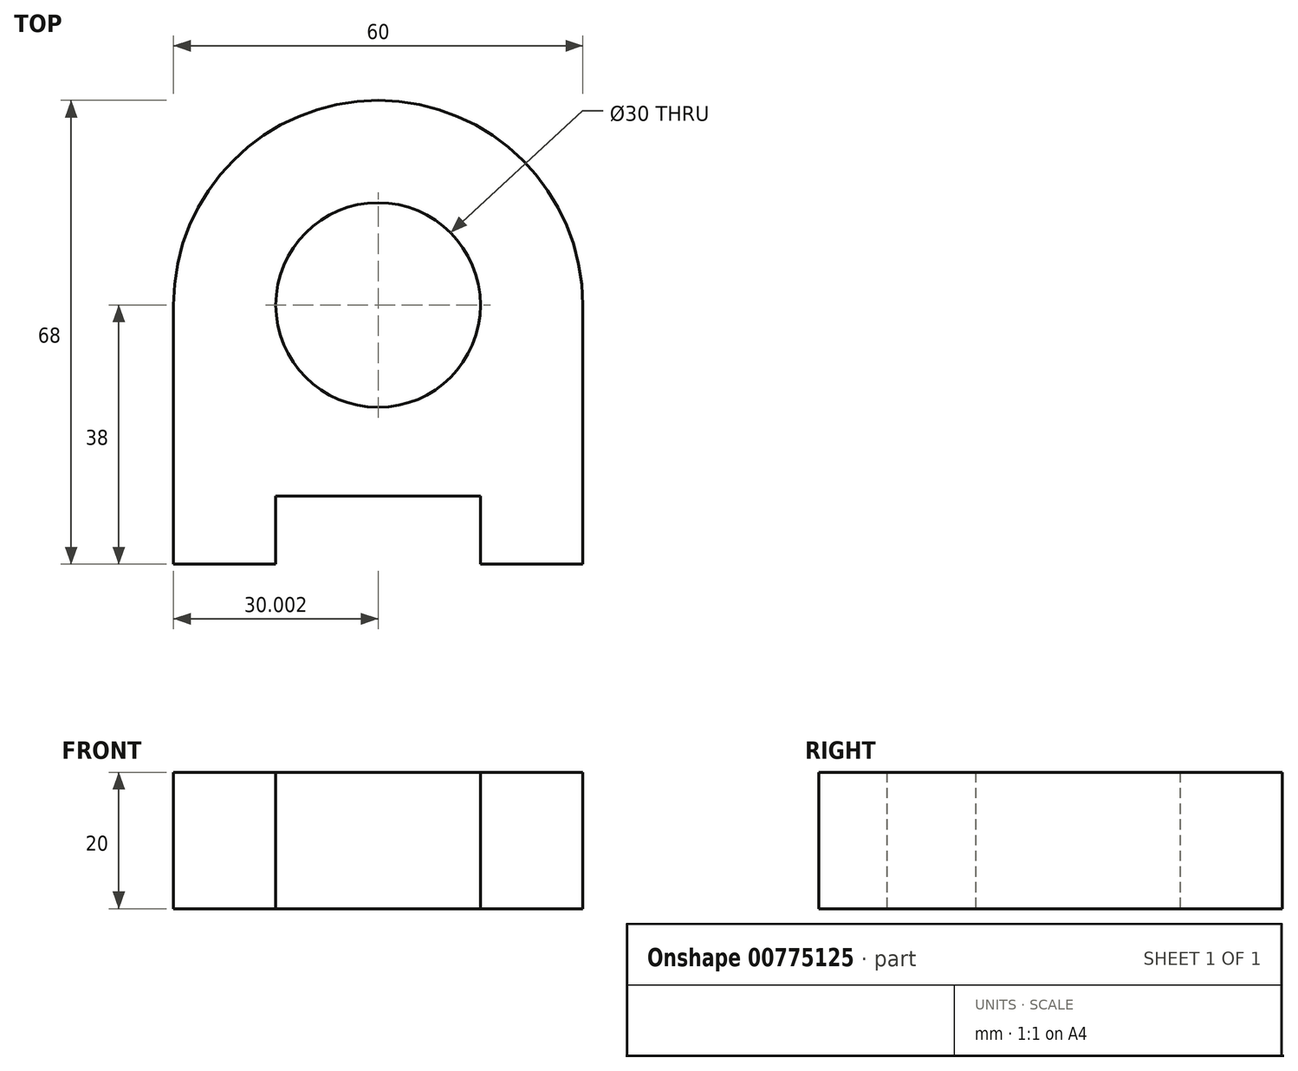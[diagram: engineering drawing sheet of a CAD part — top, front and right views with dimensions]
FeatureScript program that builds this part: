
annotation { "Feature Type Name" : "Feature", "Feature Type Description" : "" }
export const myFeature = defineFeature(function(context is Context, id is Id, definition is map)
    precondition{}
    {
        {
            var Q0;
            Q0=qCreatedBy(makeId("Top.planeOp"),FACE);
            var sketch = newSketch(context, id + "F0", { "sketchPlane" : qUnion([Q0])});
            skLineSegment(sketch, "E0.top", {"start": v(-348.27, 0) * mm, "end": v(-333.27, 0) * mm});
            skLineSegment(sketch, "E0.left", {"start": v(-348.27, 38) * mm, "end": v(-348.27, 0) * mm});
            skLineSegment(sketch, "E0.right", {"start": v(-288.27, 38) * mm, "end": v(-288.27, 0) * mm});
            skArc(sketch, "E1", {"start": v(-288.27, 38) * mm, "mid": v(-318.27, 68) * mm, "end": v(-348.27, 38) * mm});
            skCircle(sketch, "E2", {"center": v(-318.27, 38) * mm, "radius": 15 * mm});
            skLineSegment(sketch, "E3", {"start": v(-303.27, 10) * mm, "end": v(-303.27, 0) * mm});
            skLineSegment(sketch, "E4", {"start": v(-333.27, 10) * mm, "end": v(-333.27, 0) * mm});
            skLineSegment(sketch, "E5", {"start": v(-333.27, 10) * mm, "end": v(-303.27, 10) * mm});
            skLineSegment(sketch, "E6.trimOffspring", {"start": v(-303.27, 0) * mm, "end": v(-288.27, 0) * mm});
            skSolve(sketch);
        }
        {
            var Q0;
            Q0=makeQuery(id+"F0.imprint","IMPRINT",FACE,{"disambiguationData":[TD([[makeQuery(id+"F0.imprint","IMPRINT",EDGE,{"derivedFrom":sQuery(id+"F0.wireOp",EDGE,"E0.top")}),1.0]])]});
            extrude(context, id + "F1", {"entities" : qUnion([Q0]), "depth" : 20 * mm, "offsetDistance" : 25 * mm});
        }
    });
